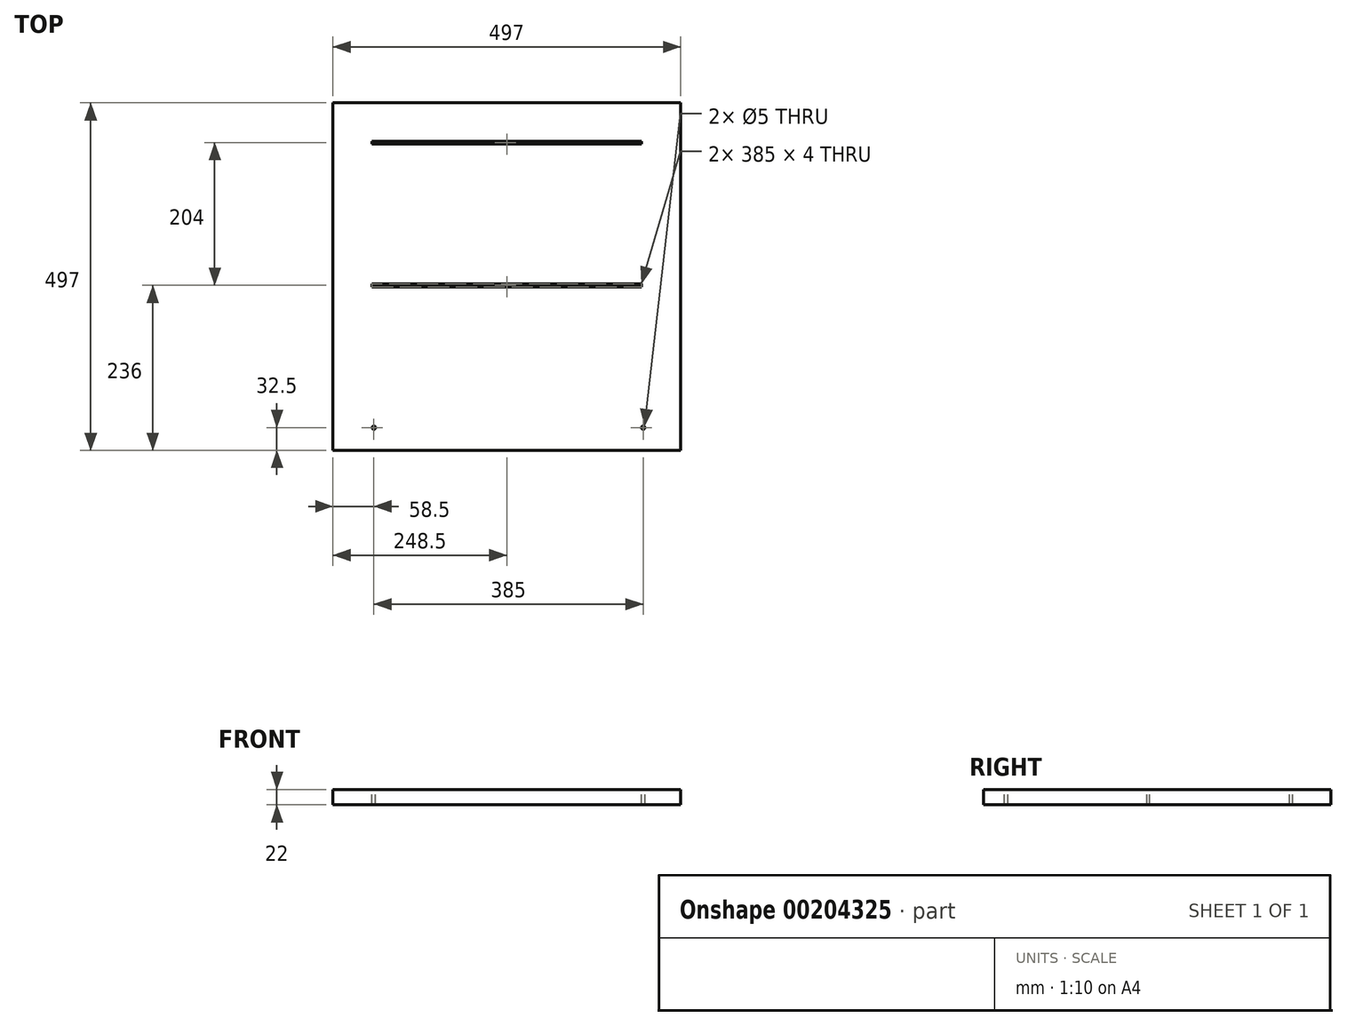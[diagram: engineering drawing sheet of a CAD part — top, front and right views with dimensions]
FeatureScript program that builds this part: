
annotation { "Feature Type Name" : "Feature", "Feature Type Description" : "" }
export const myFeature = defineFeature(function(context is Context, id is Id, definition is map)
    precondition{}
    {
        {
            var Q0;
            Q0=qCreatedBy(makeId("Top.planeOp"),FACE);
            var sketch = newSketch(context, id + "F0", { "sketchPlane" : qUnion([Q0])});
            skLineSegment(sketch, "E0.bottom", {"start": v(0, 0) * mm, "end": v(497, 0) * mm});
            skLineSegment(sketch, "E0.top", {"start": v(0, 497) * mm, "end": v(497, 497) * mm});
            skLineSegment(sketch, "E0.left", {"start": v(0, 0) * mm, "end": v(0, 497) * mm});
            skLineSegment(sketch, "E0.right", {"start": v(497, 0) * mm, "end": v(497, 497) * mm});
            skSolve(sketch);
        }
        {
            var Q0;
            Q0=makeQuery(id+"F0.imprint","IMPRINT",FACE,{"disambiguationData":[TD([[makeQuery(id+"F0.imprint","IMPRINT",EDGE,{"derivedFrom":sQuery(id+"F0.wireOp",EDGE,"E0.bottom")}),1.0]])]});
            extrude(context, id + "F1", {"entities" : qUnion([Q0]), "depth" : 22 * mm});
        }
        {
            var Q0;
            Q0=makeQuery(id+"F1.opExtrude","CAP_FACE",FACE,{"disambiguationData":[OSD([sQuery(id+"F0.wireOp",EDGE,"E0.bottom"),sQuery(id+"F0.wireOp",EDGE,"E0.top"),sQuery(id+"F0.wireOp",EDGE,"E0.left"),sQuery(id+"F0.wireOp",EDGE,"E0.right")])],"isStart":false});
            var sketch = newSketch(context, id + "F2", { "sketchPlane" : qUnion([Q0])});
            skLineSegment(sketch, "E1.bottom", {"start": v(56, 442) * mm, "end": v(441, 442) * mm});
            skLineSegment(sketch, "E1.top", {"start": v(56, 438) * mm, "end": v(441, 438) * mm});
            skLineSegment(sketch, "E1.left", {"start": v(56, 442) * mm, "end": v(56, 438) * mm});
            skLineSegment(sketch, "E1.right", {"start": v(441, 442) * mm, "end": v(441, 438) * mm});
            skCircle(sketch, "E2", {"center": v(58.5, 32.5) * mm, "radius": 2.5 * mm});
            skCircle(sketch, "E3", {"center": v(443.5, 32.5) * mm, "radius": 2.5 * mm});
            skLineSegment(sketch, "E4.bottom", {"start": v(56, 234) * mm, "end": v(441, 234) * mm});
            skLineSegment(sketch, "E4.top", {"start": v(56, 238) * mm, "end": v(441, 238) * mm});
            skLineSegment(sketch, "E4.left", {"start": v(56, 234) * mm, "end": v(56, 238) * mm});
            skLineSegment(sketch, "E4.right", {"start": v(441, 234) * mm, "end": v(441, 238) * mm});
            skSolve(sketch);
        }
        {
            var Q0;
            Q0 = qSketchRegion(id + "F2", true);
            extrude(context, id + "F3", {"entities" : qUnion([Q0]), "operationType" : NewBodyOperationType.REMOVE, "endBound" : BoundingType.UP_TO_NEXT, "oppositeDirection" : true, "depth" : 25 * mm});
        }
    });
